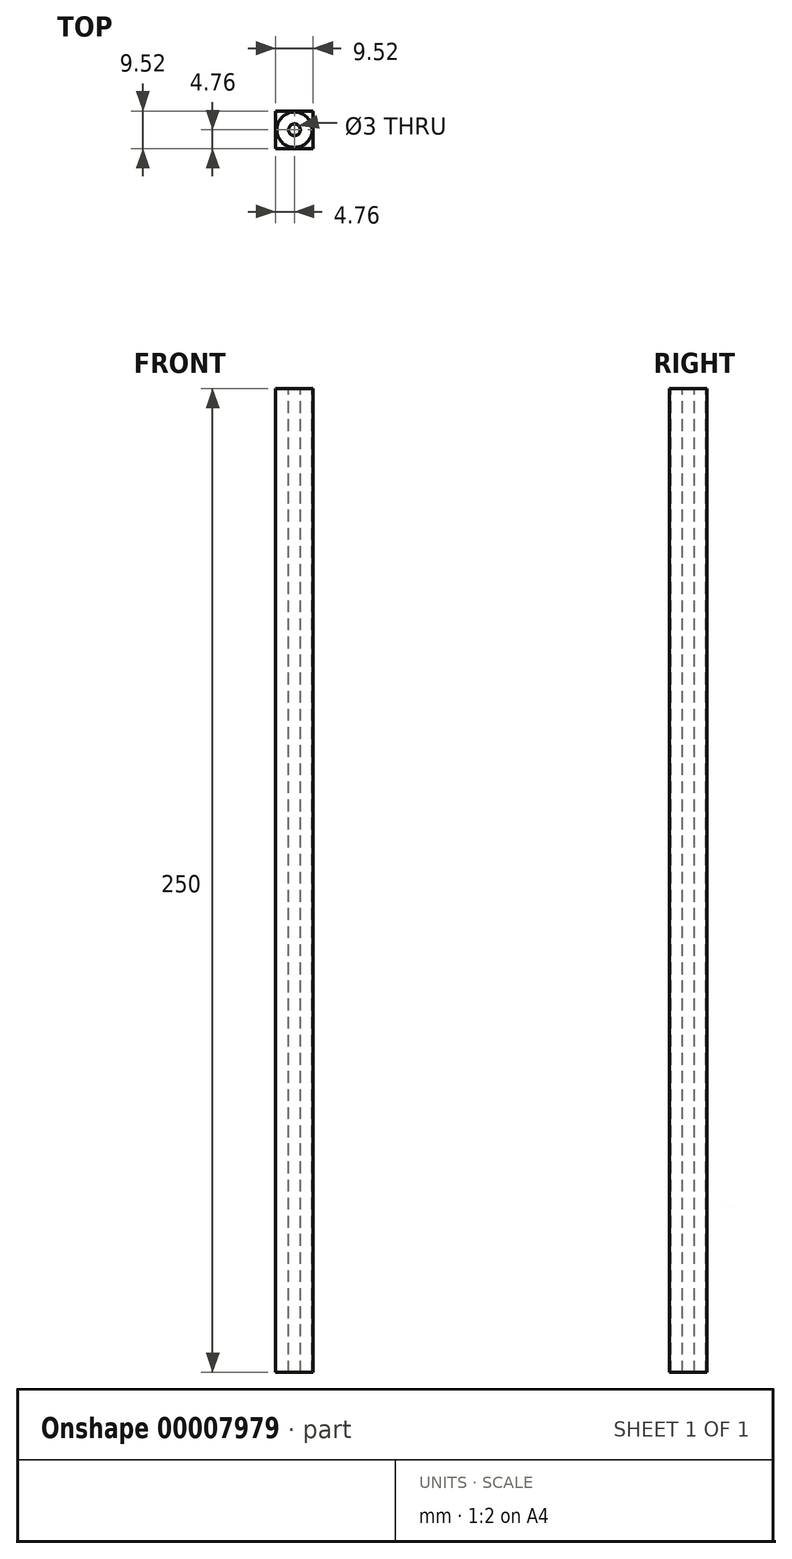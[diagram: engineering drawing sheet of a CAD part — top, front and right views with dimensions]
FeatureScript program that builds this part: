
annotation { "Feature Type Name" : "Feature", "Feature Type Description" : "" }
export const myFeature = defineFeature(function(context is Context, id is Id, definition is map)
    precondition{}
    {
        {
            var Q0;
            Q0=qCreatedBy(makeId("Top.planeOp"),FACE);
            var sketch = newSketch(context, id + "F0", { "sketchPlane" : qUnion([Q0])});
            skCircle(sketch, "E0", {"center": v(0, 0) * mm, "radius": 4.5 * mm});
            skCircle(sketch, "E1", {"center": v(0, 0) * mm, "radius": 1.5 * mm});
            skLineSegment(sketch, "E2.bottom", {"start": v(4.76, -4.76) * mm, "end": v(-4.76, -4.76) * mm});
            skLineSegment(sketch, "E2.top", {"start": v(4.76, 4.76) * mm, "end": v(-4.76, 4.76) * mm});
            skLineSegment(sketch, "E2.left", {"start": v(4.76, -4.76) * mm, "end": v(4.76, 4.76) * mm});
            skLineSegment(sketch, "E2.right", {"start": v(-4.76, -4.76) * mm, "end": v(-4.76, 4.76) * mm});
            skSolve(sketch);
        }
        {
            var Q0;
            Q0=makeQuery(id+"F0.imprint","IMPRINT",FACE,{"disambiguationData":[TD([[makeQuery(id+"F0.imprint","IMPRINT",EDGE,{"derivedFrom":sQuery(id+"F0.wireOp",EDGE,"E0")}),1.0]])]});
            extrude(context, id + "F1", {"entities" : qUnion([Q0]), "oppositeDirection" : true, "depth" : 250 * mm});
        }
        {
            var Q0;
            Q0=makeQuery(id+"F0.imprint","IMPRINT",FACE,{"disambiguationData":[TD([[makeQuery(id+"F0.imprint","IMPRINT",EDGE,{"derivedFrom":sQuery(id+"F0.wireOp",EDGE,"E0")}),-1.0]])]});
            var Q1;
            Q1=makeQuery(id+"F0.imprint","IMPRINT",FACE,{"disambiguationData":[TD([[makeQuery(id+"F0.imprint","IMPRINT",EDGE,{"derivedFrom":sQuery(id+"F0.wireOp",EDGE,"E0")}),1.0]])]});
            var Q2;
            Q2=makeQuery(id+"F0.imprint","IMPRINT",FACE,{"disambiguationData":[TD([[makeQuery(id+"F0.imprint","IMPRINT",EDGE,{"derivedFrom":sQuery(id+"F0.wireOp",EDGE,"E1")}),1.0]])]});
            extrude(context, id + "F2", {"entities" : qUnion([Q0, Q1, Q2]), "oppositeDirection" : true, "depth" : 250 * mm});
        }
        {
            var Q0;
            Q0=makeQuery(id+"F2.opExtrude","SWEPT_BODY",BODY,{"disambiguationData":[OSD([sQuery(id+"F0.wireOp",EDGE,"E2.bottom"),sQuery(id+"F0.wireOp",EDGE,"E2.top"),sQuery(id+"F0.wireOp",EDGE,"E2.left"),sQuery(id+"F0.wireOp",EDGE,"E2.right")])]});
            transform(context, id + "F3", {"entities" : qUnion([Q0]), "transformType" : TransformType.TRANSLATION_3D, "dx" : 0 * mm, "dy" : 0 * mm, "dz" : 0 * mm, "makeCopy" : true});
        }
    });
